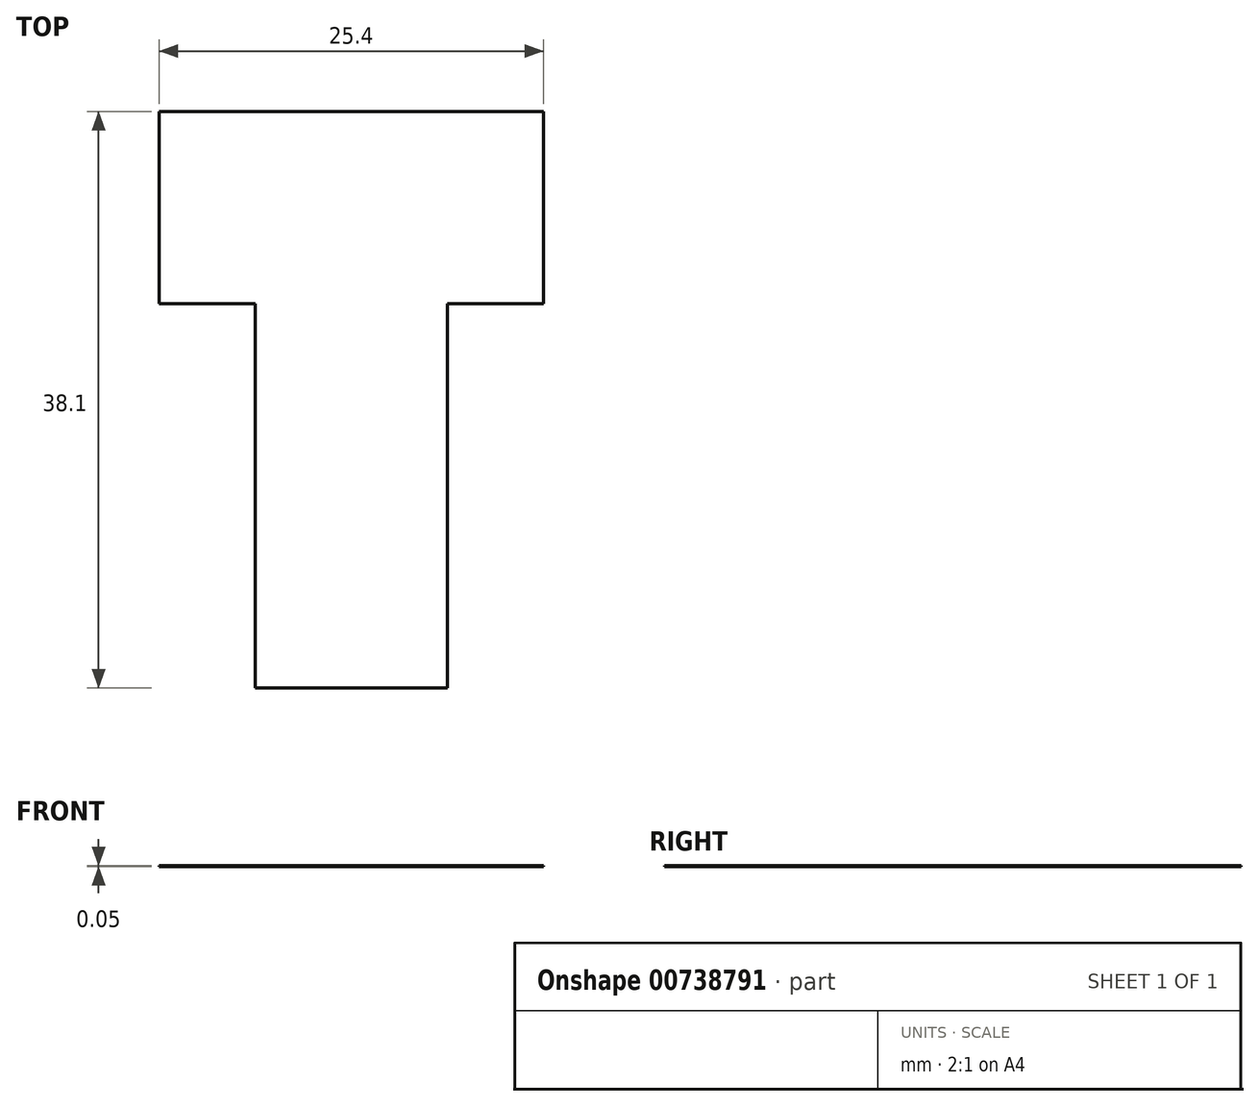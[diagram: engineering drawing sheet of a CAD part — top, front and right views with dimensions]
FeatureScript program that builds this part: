
annotation { "Feature Type Name" : "Feature", "Feature Type Description" : "" }
export const myFeature = defineFeature(function(context is Context, id is Id, definition is map)
    precondition{}
    {
        {
            var Q0;
            Q0=qCreatedBy(makeId("Top.planeOp"),FACE);
            var sketch = newSketch(context, id + "F0", { "sketchPlane" : qUnion([Q0])});
            skLineSegment(sketch, "E0", {"start": v(-11.45, 26.04) * mm, "end": v(-11.45, 13.34) * mm});
            skLineSegment(sketch, "E1", {"start": v(-11.45, 13.34) * mm, "end": v(-5.1, 13.34) * mm});
            skLineSegment(sketch, "E2", {"start": v(-5.1, 13.34) * mm, "end": v(-5.1, -12.06) * mm});
            skLineSegment(sketch, "E3", {"start": v(-5.1, -12.06) * mm, "end": v(7.6, -12.06) * mm});
            skLineSegment(sketch, "E4", {"start": v(7.6, -12.06) * mm, "end": v(7.6, 13.34) * mm});
            skLineSegment(sketch, "E5", {"start": v(7.6, 13.34) * mm, "end": v(13.95, 13.34) * mm});
            skLineSegment(sketch, "E6", {"start": v(13.95, 13.34) * mm, "end": v(13.95, 26.04) * mm});
            skLineSegment(sketch, "E7", {"start": v(13.95, 26.04) * mm, "end": v(-11.45, 26.04) * mm});
            skSolve(sketch);
        }
        {
            var Q0;
            Q0 = qSketchRegion(id + "F0", true);
            extrude(context, id + "F1", {"entities" : qUnion([Q0]), "depth" : 5 / 101.6 * mm, "offsetDistance" : 25.4 * mm});
        }
    });
